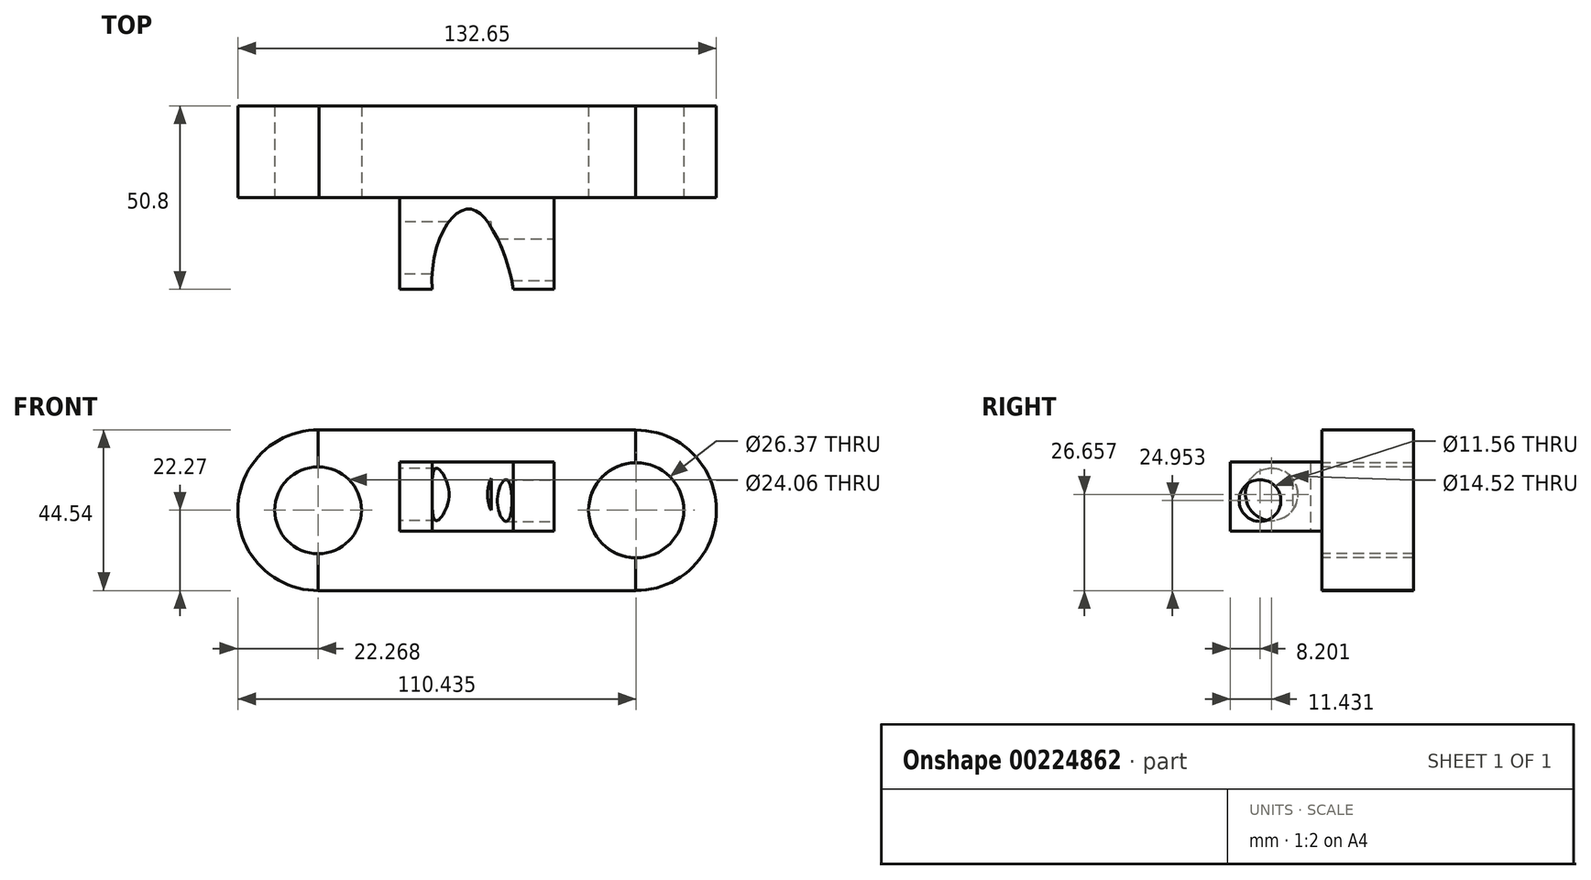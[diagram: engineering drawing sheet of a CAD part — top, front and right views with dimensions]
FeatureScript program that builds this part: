
annotation { "Feature Type Name" : "Feature", "Feature Type Description" : "" }
export const myFeature = defineFeature(function(context is Context, id is Id, definition is map)
    precondition{}
    {
        {
            var Q0;
            Q0=qCreatedBy(makeId("Front.planeOp"),FACE);
            var sketch = newSketch(context, id + "F0", { "sketchPlane" : qUnion([Q0])});
            skLineSegment(sketch, "E0.bottom", {"start": v(-44, 22.27) * mm, "end": v(44, 22.27) * mm});
            skLineSegment(sketch, "E0.top", {"start": v(-44, -22.27) * mm, "end": v(44, -22.27) * mm});
            skLineSegment(sketch, "E0.left", {"start": v(-44, 22.27) * mm, "end": v(-44, -22.27) * mm});
            skLineSegment(sketch, "E0.right", {"start": v(44, 22.27) * mm, "end": v(44, -22.27) * mm});
            skPoint(sketch, "E0.middle", {"position": v(0, 0) * mm});
            skSolve(sketch);
        }
        {
            var Q0;
            Q0=makeQuery(id+"F0.imprint","IMPRINT",FACE,{"disambiguationData":[TD([[makeQuery(id+"F0.imprint","IMPRINT",EDGE,{"derivedFrom":sQuery(id+"F0.wireOp",EDGE,"E0.bottom")}),-1.0]])]});
            var sketch = newSketch(context, id + "F1", { "sketchPlane" : qUnion([Q0])});
            skCircle(sketch, "E1", {"center": v(-44, 0) * mm, "radius": 22.27 * mm});
            skSolve(sketch);
        }
        {
            var Q0;
            Q0=makeQuery(id+"F0.imprint","IMPRINT",FACE,{"disambiguationData":[TD([[makeQuery(id+"F0.imprint","IMPRINT",EDGE,{"derivedFrom":sQuery(id+"F0.wireOp",EDGE,"E0.bottom")}),-1.0]])]});
            var sketch = newSketch(context, id + "F2", { "sketchPlane" : qUnion([Q0])});
            skCircle(sketch, "E2", {"center": v(44.18, 0) * mm, "radius": 22.22 * mm});
            skSolve(sketch);
        }
        {
            var Q0;
            Q0=makeQuery(id+"F0.imprint","IMPRINT",FACE,{"disambiguationData":[TD([[makeQuery(id+"F0.imprint","IMPRINT",EDGE,{"derivedFrom":sQuery(id+"F0.wireOp",EDGE,"E0.bottom")}),-1.0]])]});
            var Q1;
            {var subQ5=makeQuery(id+"F0.imprint","IMPRINT",EDGE,{"derivedFrom":sQuery(id+"F0.wireOp",EDGE,"E0.right")});Q1=makeQuery(id+"F1.imprint","IMPRINT",FACE,{"disambiguationData":[TD([[makeQuery(id+"F1.imprint","IMPRINT",EDGE,{"derivedFrom":subQ5}),-1.0]])]});}
            var Q2;
            {var subQ5=makeQuery(id+"F0.imprint","IMPRINT",EDGE,{"derivedFrom":sQuery(id+"F0.wireOp",EDGE,"E0.left")});Q2=makeQuery(id+"F1.imprint","IMPRINT",FACE,{"disambiguationData":[TD([[makeQuery(id+"F1.imprint","IMPRINT",EDGE,{"derivedFrom":subQ5}),1.0]])]});}
            var Q3;
            {var subQ0=sQuery(id+"F2.wireOp",EDGE,"E2");var subQ1=makeQuery(id+"F0.imprint","IMPRINT",EDGE,{"derivedFrom":sQuery(id+"F0.wireOp",EDGE,"E0.right")});var subQ2=makeQuery(id+"F2.imprint","INTERSECT",VERTEX,{"disambiguationData":[OD(0.0)],"derivedFrom":[subQ1,subQ0]});Q3=makeQuery(id+"F2.imprint","IMPRINT",FACE,{"disambiguationData":[TD([[makeQuery(id+"F2.imprint","IMPRINT",EDGE,{"disambiguationData":[TD([[subQ2,1.0]])],"derivedFrom":subQ0}),1.0]])]});}
            var Q4;
            {var subQ0=sQuery(id+"F2.wireOp",EDGE,"E2");var subQ1=makeQuery(id+"F0.imprint","IMPRINT",EDGE,{"derivedFrom":sQuery(id+"F0.wireOp",EDGE,"E0.right")});var subQ2=makeQuery(id+"F2.imprint","INTERSECT",VERTEX,{"disambiguationData":[OD(0.0)],"derivedFrom":[subQ1,subQ0]});Q4=makeQuery(id+"F2.imprint","IMPRINT",FACE,{"disambiguationData":[TD([[makeQuery(id+"F2.imprint","IMPRINT",EDGE,{"disambiguationData":[TD([[subQ2,-1.0]])],"derivedFrom":subQ0}),1.0]])]});}
            var Q5;
            {var subQ1=makeQuery(id+"F0.imprint","IMPRINT",EDGE,{"derivedFrom":sQuery(id+"F0.wireOp",EDGE,"E0.bottom")});Q5=makeQuery(id+"F2.imprint","IMPRINT",FACE,{"disambiguationData":[TD([[makeQuery(id+"F2.imprint","IMPRINT",EDGE,{"derivedFrom":subQ1}),-1.0]])]});}
            var Q6;
            {var subQ5=makeQuery(id+"F0.imprint","IMPRINT",EDGE,{"derivedFrom":sQuery(id+"F0.wireOp",EDGE,"E0.left")});Q6=makeQuery(id+"F1.imprint","IMPRINT",FACE,{"disambiguationData":[TD([[makeQuery(id+"F1.imprint","IMPRINT",EDGE,{"derivedFrom":subQ5}),-1.0]])]});}
            extrude(context, id + "F3", {"entities" : qUnion([Q0, Q1, Q2, Q3, Q4, Q5, Q6]), "depth" : 25.4 * mm});
        }
        {
            var Q0;
            Q0=makeQuery(id+"F3.opExtrude","CAP_FACE",FACE,{"disambiguationData":[OSD([sQuery(id+"F0.wireOp",EDGE,"E0.bottom"),sQuery(id+"F0.wireOp",EDGE,"E0.top"),sQuery(id+"F0.wireOp",EDGE,"E0.right"),sQuery(id+"F1.wireOp",EDGE,"E1")])],"isStart":false});
            var sketch = newSketch(context, id + "F4", { "sketchPlane" : qUnion([Q0])});
            skCircle(sketch, "E3", {"center": v(-44, 0) * mm, "radius": 12.03 * mm});
            skSolve(sketch);
        }
        {
            var Q0;
            Q0=makeQuery(id+"F4.imprint","IMPRINT",FACE,{"disambiguationData":[TD([[makeQuery(id+"F4.imprint","IMPRINT",EDGE,{"derivedFrom":sQuery(id+"F4.wireOp",EDGE,"E3")}),1.0]])]});
            extrude(context, id + "F5", {"entities" : qUnion([Q0]), "operationType" : NewBodyOperationType.REMOVE, "oppositeDirection" : true, "depth" : 25.4 * mm, "hasSecondDirection" : true, "secondDirectionOppositeDirection" : false, "secondDirectionDepth" : 25.4 * mm});
        }
        {
            var Q0;
            Q0=makeQuery(id+"F3.opExtrude","CAP_FACE",FACE,{"disambiguationData":[OSD([sQuery(id+"F0.wireOp",EDGE,"E0.bottom"),sQuery(id+"F0.wireOp",EDGE,"E0.top"),sQuery(id+"F0.wireOp",EDGE,"E0.left"),sQuery(id+"F0.wireOp",EDGE,"E0.right"),sQuery(id+"F2.wireOp",EDGE,"E2")])],"isStart":false});
            var sketch = newSketch(context, id + "F6", { "sketchPlane" : qUnion([Q0])});
            skCircle(sketch, "E4", {"center": v(44.18, 0) * mm, "radius": 13.18 * mm});
            skSolve(sketch);
        }
        {
            var Q0;
            Q0=makeQuery(id+"F6.imprint","IMPRINT",FACE,{"disambiguationData":[TD([[makeQuery(id+"F6.imprint","IMPRINT",EDGE,{"derivedFrom":sQuery(id+"F6.wireOp",EDGE,"E4")}),1.0]])]});
            extrude(context, id + "F7", {"entities" : qUnion([Q0]), "operationType" : NewBodyOperationType.REMOVE, "oppositeDirection" : true, "depth" : 25.4 * mm});
        }
        {
            var Q0;
            Q0=makeQuery(id+"F3.opExtrude","CAP_FACE",FACE,{"disambiguationData":[OSD([sQuery(id+"F0.wireOp",EDGE,"E0.bottom"),sQuery(id+"F0.wireOp",EDGE,"E0.top"),sQuery(id+"F0.wireOp",EDGE,"E0.left"),sQuery(id+"F0.wireOp",EDGE,"E0.right")])],"isStart":false});
            var sketch = newSketch(context, id + "F8", { "sketchPlane" : qUnion([Q0])});
            skLineSegment(sketch, "E5.bottom", {"start": v(-21.44, -5.78) * mm, "end": v(21.44, -5.78) * mm});
            skLineSegment(sketch, "E5.top", {"start": v(-21.44, 13.35) * mm, "end": v(21.44, 13.35) * mm});
            skLineSegment(sketch, "E5.left", {"start": v(-21.44, -5.78) * mm, "end": v(-21.44, 13.35) * mm});
            skLineSegment(sketch, "E5.right", {"start": v(21.44, -5.78) * mm, "end": v(21.44, 13.35) * mm});
            skPoint(sketch, "E5.middle", {"position": v(0, 3.79) * mm});
            skSolve(sketch);
        }
        {
            var Q0;
            Q0=makeQuery(id+"F8.imprint","IMPRINT",FACE,{"disambiguationData":[TD([[makeQuery(id+"F8.imprint","IMPRINT",EDGE,{"derivedFrom":sQuery(id+"F8.wireOp",EDGE,"E5.bottom")}),1.0]])]});
            extrude(context, id + "F9", {"entities" : qUnion([Q0]), "depth" : 25.4 * mm});
        }
        {
            var Q0;
            Q0=makeQuery(id+"F9.opExtrude","SWEPT_FACE",FACE,{"disambiguationData":[OSD([sQuery(id+"F8.wireOp",EDGE,"E5.bottom")])]});
            var sketch = newSketch(context, id + "F10", { "sketchPlane" : qUnion([Q0])});
            skFitSpline(sketch, "E6", {"points": [v(-8.7, 60.03) * mm, v(-10.02, 36.2) * mm, v(-2.22, 28.59) * mm, v(5.34, 36.05) * mm, v(8.31, 59.99) * mm, v(-8.7, 60.03) * mm]});
            skSolve(sketch);
        }
        {
            var Q0;
            {var subQ0=sQuery(id+"F10.wireOp",EDGE,"E6");var subQ1=makeQuery(id+"F9.opExtrude","CAP_EDGE",EDGE,{"disambiguationData":[OSD([sQuery(id+"F8.wireOp",EDGE,"E5.bottom")])],"isStart":false});var subQ2=makeQuery(id+"F10.imprint","INTERSECT",VERTEX,{"disambiguationData":[OD(0.0)],"derivedFrom":[subQ1,subQ0]});Q0=makeQuery(id+"F10.imprint","IMPRINT",FACE,{"disambiguationData":[TD([[makeQuery(id+"F10.imprint","IMPRINT",EDGE,{"disambiguationData":[TD([[subQ2,-1.0]])],"derivedFrom":subQ0}),1.0]])]});}
            var Q1;
            {var subQ0=sQuery(id+"F10.wireOp",EDGE,"E6");var subQ1=makeQuery(id+"F9.opExtrude","CAP_EDGE",EDGE,{"disambiguationData":[OSD([sQuery(id+"F8.wireOp",EDGE,"E5.bottom")])],"isStart":false});var subQ2=makeQuery(id+"F10.imprint","INTERSECT",VERTEX,{"disambiguationData":[OD(0.0)],"derivedFrom":[subQ1,subQ0]});Q1=makeQuery(id+"F10.imprint","IMPRINT",FACE,{"disambiguationData":[TD([[makeQuery(id+"F10.imprint","IMPRINT",EDGE,{"disambiguationData":[TD([[subQ2,1.0]])],"derivedFrom":subQ0}),1.0]])]});}
            extrude(context, id + "F11", {"entities" : qUnion([Q0, Q1]), "operationType" : NewBodyOperationType.REMOVE, "oppositeDirection" : true, "depth" : 25.4 * mm});
        }
        {
            var Q0;
            Q0=makeQuery(id+"F9.opExtrude","SWEPT_FACE",FACE,{"disambiguationData":[OSD([sQuery(id+"F8.wireOp",EDGE,"E5.right")])]});
            var sketch = newSketch(context, id + "F12", { "sketchPlane" : qUnion([Q0])});
            skCircle(sketch, "E7", {"center": v(-42.6, 2.68) * mm, "radius": 5.78 * mm});
            skSolve(sketch);
        }
        {
            var Q0;
            Q0=makeQuery(id+"F12.imprint","IMPRINT",FACE,{"disambiguationData":[TD([[makeQuery(id+"F12.imprint","IMPRINT",EDGE,{"derivedFrom":sQuery(id+"F12.wireOp",EDGE,"E7")}),1.0]])]});
            extrude(context, id + "F13", {"entities" : qUnion([Q0]), "operationType" : NewBodyOperationType.REMOVE, "oppositeDirection" : true, "depth" : 25.4 * mm});
        }
        {
            var Q0;
            Q0=makeQuery(id+"F9.opExtrude","SWEPT_FACE",FACE,{"disambiguationData":[OSD([sQuery(id+"F8.wireOp",EDGE,"E5.left")])]});
            var sketch = newSketch(context, id + "F14", { "sketchPlane" : qUnion([Q0])});
            skCircle(sketch, "E8", {"center": v(39.37, 4.39) * mm, "radius": 7.26 * mm});
            skSolve(sketch);
        }
        {
            var Q0;
            Q0=makeQuery(id+"F14.imprint","IMPRINT",FACE,{"disambiguationData":[TD([[makeQuery(id+"F14.imprint","IMPRINT",EDGE,{"derivedFrom":sQuery(id+"F14.wireOp",EDGE,"E8")}),1.0]])]});
            extrude(context, id + "F15", {"entities" : qUnion([Q0]), "operationType" : NewBodyOperationType.REMOVE, "oppositeDirection" : true, "depth" : 25.4 * mm});
        }
    });
